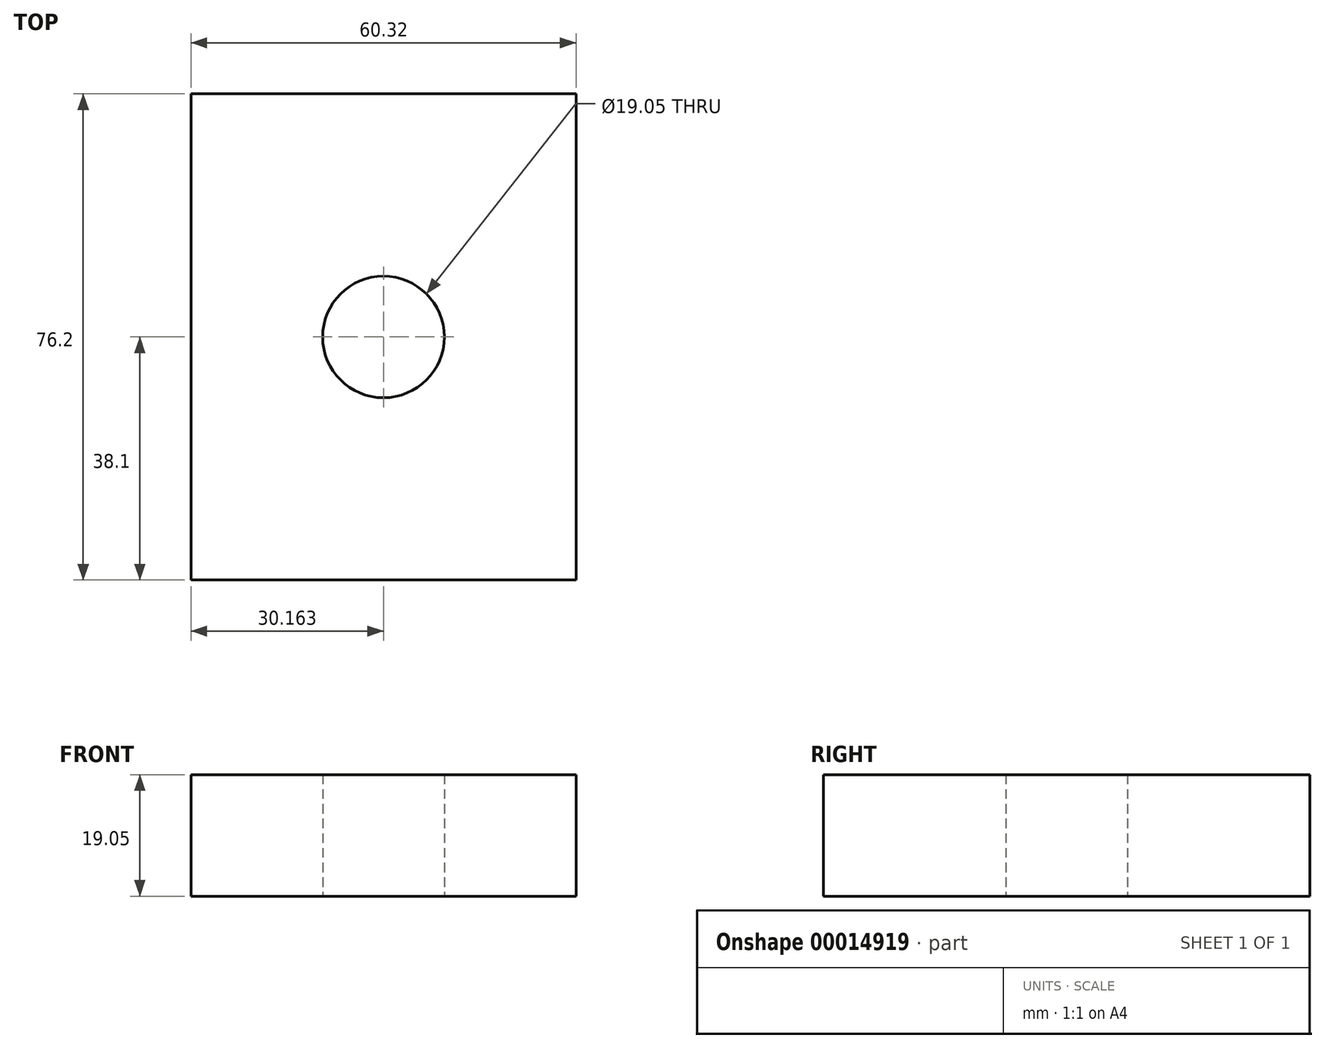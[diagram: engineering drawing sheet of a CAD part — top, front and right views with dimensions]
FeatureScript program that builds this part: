
annotation { "Feature Type Name" : "Feature", "Feature Type Description" : "" }
export const myFeature = defineFeature(function(context is Context, id is Id, definition is map)
    precondition{}
    {
        {
            var Q0;
            Q0=qCreatedBy(makeId("Top.planeOp"),FACE);
            var sketch = newSketch(context, id + "F0", { "sketchPlane" : qUnion([Q0])});
            skLineSegment(sketch, "E0.bottom", {"start": v(0, 76.2) * mm, "end": v(60.33, 76.2) * mm});
            skLineSegment(sketch, "E0.top", {"start": v(0, 0) * mm, "end": v(60.33, 0) * mm});
            skLineSegment(sketch, "E0.left", {"start": v(0, 76.2) * mm, "end": v(0, 0) * mm});
            skLineSegment(sketch, "E0.right", {"start": v(60.32, 76.2) * mm, "end": v(60.33, 0) * mm});
            skCircle(sketch, "E1", {"center": v(30.16, 38.1) * mm, "radius": 9.53 * mm});
            skSolve(sketch);
        }
        {
            var Q0;
            Q0=makeQuery(id+"F0.imprint","IMPRINT",FACE,{"disambiguationData":[TD([[makeQuery(id+"F0.imprint","IMPRINT",EDGE,{"derivedFrom":sQuery(id+"F0.wireOp",EDGE,"E0.bottom")}),-1.0]])]});
            extrude(context, id + "F1", {"entities" : qUnion([Q0]), "depth" : 19.05 * mm});
        }
    });
